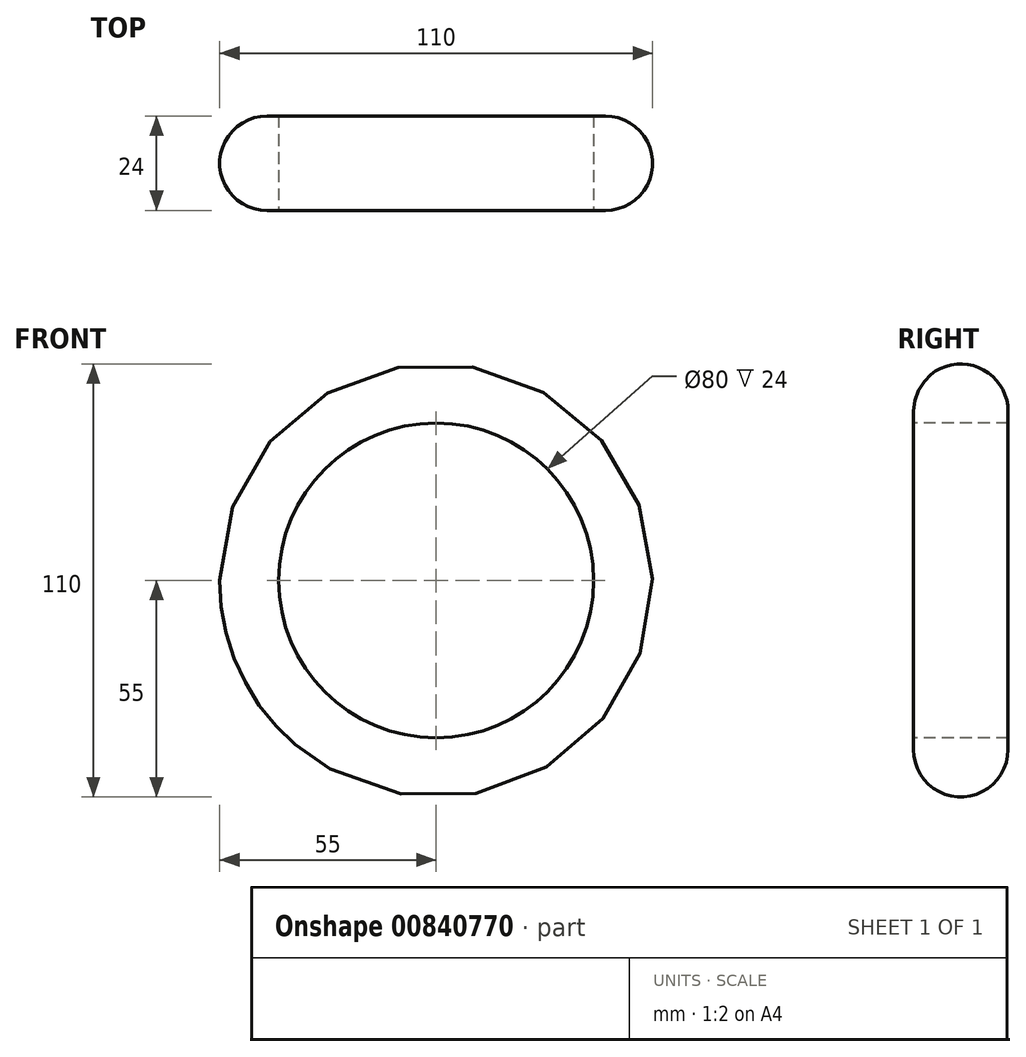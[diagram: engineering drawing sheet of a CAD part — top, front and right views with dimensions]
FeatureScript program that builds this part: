
annotation { "Feature Type Name" : "Feature", "Feature Type Description" : "" }
export const myFeature = defineFeature(function(context is Context, id is Id, definition is map)
    precondition{}
    {
        {
            var Q0;
            Q0=qCreatedBy(makeId("Front.planeOp"),FACE);
            var sketch = newSketch(context, id + "F0", { "sketchPlane" : qUnion([Q0])});
            skCircle(sketch, "E0", {"center": v(0, 0) * mm, "radius": 40 * mm});
            skSolve(sketch);
        }
        {
            var Q0;
            Q0=qCreatedBy(makeId("Top.planeOp"),FACE);
            var sketch = newSketch(context, id + "F1", { "sketchPlane" : qUnion([Q0])});
            skArc(sketch, "E1", {"start": v(-43, 12) * mm, "mid": v(-55, 0) * mm, "end": v(-43, -12) * mm});
            skLineSegment(sketch, "E2", {"start": v(-43, 12) * mm, "end": v(-40, 12) * mm});
            skLineSegment(sketch, "E3", {"start": v(-43, -12) * mm, "end": v(-40, -12) * mm});
            skLineSegment(sketch, "E4", {"start": v(-40, 12) * mm, "end": v(-40, -12) * mm});
            skSolve(sketch);
        }
        {
            var Q0;
            Q0=qSketchRegion(id+"F1",true);
            var Q1;
            Q1=qConstructionFilter(qBodyType(qCreatedBy(id+"F0",EDGE),BodyType.WIRE),ConstructionObject.NO);
            sweep(context, id + "F2", {"profiles" : qUnion([Q0]), "path" : qUnion([Q1])});
        }
        {
            var Q0;
            Q0=qCreatedBy(makeId("Right.planeOp"),FACE);
            cPlane(context, id + "F3", {"entities" : qUnion([Q0]), "cplaneType" : CPlaneType.OFFSET, "offset" : 40 * mm, "width" : 150 * mm, "height" : 150 * mm});
        }
        {
            var Q0;
            Q0=qCreatedBy(id+"F3.planeOp",FACE);
            var sketch = newSketch(context, id + "F4", { "sketchPlane" : qUnion([Q0])});
            skLineSegment(sketch, "E5", {"start": v(0, 0) * mm, "end": v(0, 8.5) * mm});
            skLineSegment(sketch, "E6", {"start": v(0, 8.5) * mm, "end": v(0, -9.5) * mm});
            skPoint(sketch, "E7.0.right.start.orphan", {"position": v(-7, 8.5) * mm});
            skArc(sketch, "E8.0.startCap", {"start": v(-2.5, 8.5) * mm, "mid": v(0, 11) * mm, "end": v(2.5, 8.5) * mm});
            skArc(sketch, "E8.0.endCap", {"start": v(2.5, -9.5) * mm, "mid": v(0, -12) * mm, "end": v(-2.5, -9.5) * mm});
            skLineSegment(sketch, "E8.0.left", {"start": v(2.5, 8.5) * mm, "end": v(2.5, -9.5) * mm});
            skLineSegment(sketch, "E8.0.right", {"start": v(-2.5, 8.5) * mm, "end": v(-2.5, -9.5) * mm});
            skSolve(sketch);
        }
        {
            var Q0;
            Q0=qCreatedBy(makeId("Right.planeOp"),FACE);
            cPlane(context, id + "F5", {"entities" : qUnion([Q0]), "cplaneType" : CPlaneType.OFFSET, "offset" : 14 * mm, "width" : 150 * mm, "height" : 150 * mm});
        }
    });
